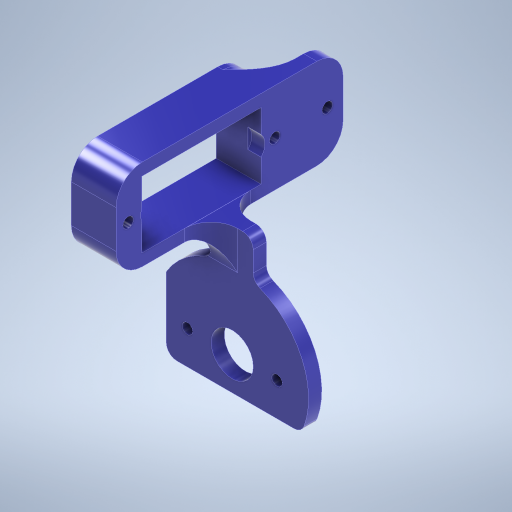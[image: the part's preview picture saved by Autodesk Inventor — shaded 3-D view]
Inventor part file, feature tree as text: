
AUTODESK INVENTOR PART (.ipt)
format: ipt  version: 2023.2 (Build 272271000, 271)  size: 426,496 bytes
history: native  units: mm
features: extrude x4, fillet x4, sketch x4
ambient origin geometry x8: Origin, YZ Plane, XZ Plane, XY Plane, X Axis, Y Axis, Z Axis, Center Point
bodies: Solid1 (feature_tree)
feature tree (12):
  extrude  "Extrusion1"  Depth=2.5mm TaperAngle=0.0deg
  extrude  "Extrusion2"  Depth=2.0mm
  fillet  "Fillet1"  Radius=2.0mm
  extrude  "Extrusion4"  Depth=2.5mm
  fillet  "Fillet2"  Radius=8.0mm
  fillet  "Fillet3"  Radius=2.5mm
  extrude  "Extrusion5"  Depth=2.0mm
  fillet  "Fillet4"  Radius=27.8mm
  sketch  "Sketch1"  dims[d0=12.6mm d2=2.5mm d3=0.0mm]
  sketch  "Sketch2"  dims[d4=29.0mm d5=17.0mm d6=2.0mm]
  sketch  "Sketch4"  dims[d7=2.0mm d8=8.0mm d9=8.0mm d10=2.5mm d11=0.0mm]
  sketch  "Sketch5"  dims[d12=5.0mm d13=2.0mm d14=27.8mm d15=8.7mm d16=2.0mm d17=2.0mm d18=12.6mm d19=11.4mm d20=5.0mm d21=12.6mm d22=22.6mm d23=2.6mm d26=6.0mm d27=0.0mm d28=2.0mm d29=4.9mm d30=3.0mm d31=5.0mm d32=17.658042mm d33=5.020146mm d34=42.428mm d35=5.0mm d36=2.5mm d37=0.0mm d38=2.0mm d24=0.5mm d25=0.872665mm]
